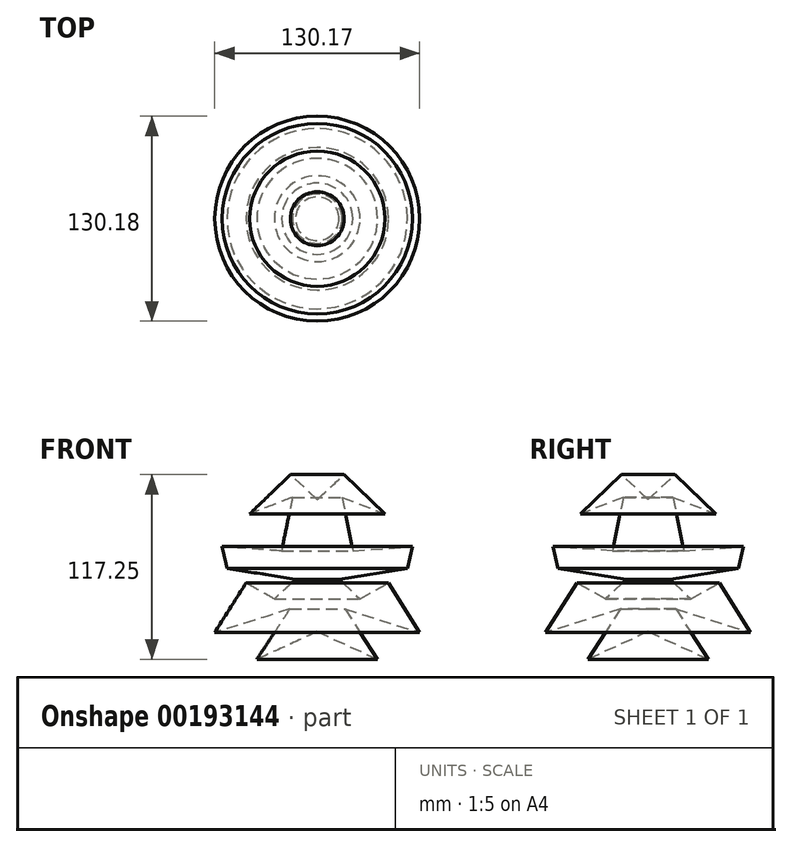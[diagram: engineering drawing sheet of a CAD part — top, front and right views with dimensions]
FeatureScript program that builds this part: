
annotation { "Feature Type Name" : "Feature", "Feature Type Description" : "" }
export const myFeature = defineFeature(function(context is Context, id is Id, definition is map)
    precondition{}
    {
        {
            var Q0;
            Q0=qCreatedBy(makeId("Front.planeOp"),FACE);
            var sketch = newSketch(context, id + "F0", { "sketchPlane" : qUnion([Q0])});
            skLineSegment(sketch, "E0", {"start": v(9.7, -42.7) * mm, "end": v(9.7, 41.31) * mm});
            skLineSegment(sketch, "E1", {"start": v(9.7, 41.31) * mm, "end": v(26.77, 57) * mm});
            skLineSegment(sketch, "E2", {"start": v(26.77, 57) * mm, "end": v(52.62, 32.08) * mm});
            skLineSegment(sketch, "E3", {"start": v(52.62, 32.08) * mm, "end": v(25.39, 42.7) * mm});
            skLineSegment(sketch, "E4", {"start": v(25.39, 42.7) * mm, "end": v(32.31, 8.54) * mm});
            skLineSegment(sketch, "E5", {"start": v(32.31, 8.54) * mm, "end": v(70.16, 11.3) * mm});
            skLineSegment(sketch, "E6", {"start": v(70.16, 11.3) * mm, "end": v(66.93, -2.54) * mm});
            skLineSegment(sketch, "E7", {"start": v(66.93, -2.54) * mm, "end": v(23.54, -9.46) * mm});
            skLineSegment(sketch, "E8", {"start": v(23.54, -9.46) * mm, "end": v(36.93, -21.93) * mm});
            skLineSegment(sketch, "E9", {"start": v(36.93, -21.93) * mm, "end": v(54.93, -11.77) * mm});
            skLineSegment(sketch, "E10", {"start": v(54.93, -11.77) * mm, "end": v(74.78, -43.16) * mm});
            skLineSegment(sketch, "E11", {"start": v(74.78, -43.16) * mm, "end": v(27.23, -28.39) * mm});
            skLineSegment(sketch, "E12", {"start": v(27.23, -28.39) * mm, "end": v(48, -60.24) * mm});
            skLineSegment(sketch, "E13", {"start": v(48, -60.24) * mm, "end": v(9.7, -42.7) * mm});
            skSolve(sketch);
        }
        {
            var Q0;
            Q0=makeQuery(id+"F0.imprint","IMPRINT",FACE,{"disambiguationData":[TD([[makeQuery(id+"F0.imprint","IMPRINT",EDGE,{"derivedFrom":sQuery(id+"F0.wireOp",EDGE,"E0")}),-1.0]])]});
            var Q1;
            Q1=sQuery(id+"F0.wireOp",EDGE,"E0");
            revolve(context, id + "F1", {"entities" : qUnion([Q0]), "axis" : qUnion([Q1]), "revolveType" : RevolveType.FULL});
        }
    });
